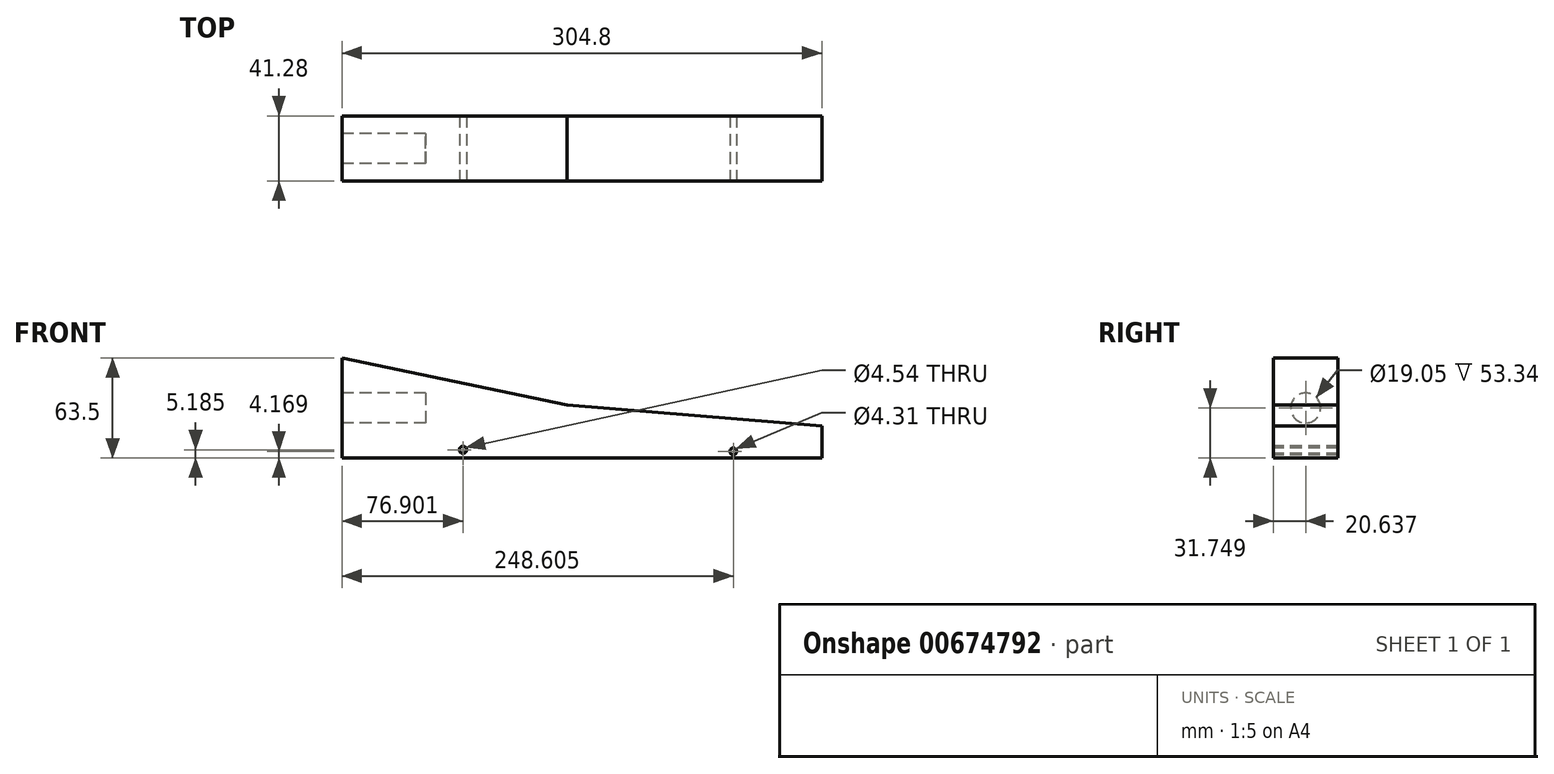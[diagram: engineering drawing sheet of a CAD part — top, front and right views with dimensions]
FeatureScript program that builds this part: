
annotation { "Feature Type Name" : "Feature", "Feature Type Description" : "" }
export const myFeature = defineFeature(function(context is Context, id is Id, definition is map)
    precondition{}
    {
        {
            var Q0;
            Q0=qCreatedBy(makeId("Front.planeOp"),FACE);
            var sketch = newSketch(context, id + "F0", { "sketchPlane" : qUnion([Q0])});
            skLineSegment(sketch, "E0", {"start": v(-67.2, 29.74) * mm, "end": v(-67.2, -33.76) * mm});
            skLineSegment(sketch, "E1", {"start": v(-67.2, -33.76) * mm, "end": v(237.6, -33.76) * mm});
            skLineSegment(sketch, "E2", {"start": v(237.6, -33.76) * mm, "end": v(237.6, -13.44) * mm});
            skLineSegment(sketch, "E3", {"start": v(237.6, -13.44) * mm, "end": v(-67.2, 29.74) * mm});
            skSolve(sketch);
        }
        {
            var Q0;
            Q0=makeQuery(id+"F0.imprint","IMPRINT",FACE,{"disambiguationData":[TD([[makeQuery(id+"F0.imprint","IMPRINT",EDGE,{"derivedFrom":sQuery(id+"F0.wireOp",EDGE,"E0")}),1.0]])]});
            extrude(context, id + "F1", {"entities" : qUnion([Q0]), "oppositeDirection" : true, "depth" : 41.27 * mm, "offsetDistance" : 25.4 * mm});
        }
        {
            var Q0;
            Q0=makeQuery(id+"F1.opExtrude","SWEPT_FACE",FACE,{"disambiguationData":[OSD([sQuery(id+"F0.wireOp",EDGE,"E0")])]});
            var sketch = newSketch(context, id + "F2", { "sketchPlane" : qUnion([Q0])});
            skCircle(sketch, "E4", {"center": v(-20.64, -2.01) * mm, "radius": 9.53 * mm});
            skPoint(sketch, "E4.centerSnap0", {"position": v(0, -2.01) * mm});
            skPoint(sketch, "E4.centerSnap1", {"position": v(-20.64, 29.74) * mm});
            skSolve(sketch);
        }
        {
            var Q0;
            Q0=makeQuery(id+"F2.imprint","IMPRINT",FACE,{"disambiguationData":[TD([[makeQuery(id+"F2.imprint","IMPRINT",EDGE,{"derivedFrom":sQuery(id+"F2.wireOp",EDGE,"E4")}),1.0]])]});
            extrude(context, id + "F3", {"entities" : qUnion([Q0]), "operationType" : NewBodyOperationType.REMOVE, "oppositeDirection" : true, "depth" : 53.34 * mm, "offsetDistance" : 25.4 * mm});
        }
        {
            var Q0;
            Q0=makeQuery(id+"F1.opExtrude","CAP_FACE",FACE,{"disambiguationData":[OSD([sQuery(id+"F0.wireOp",EDGE,"E0"),sQuery(id+"F0.wireOp",EDGE,"E1"),sQuery(id+"F0.wireOp",EDGE,"E2"),sQuery(id+"F0.wireOp",EDGE,"E3")])],"isStart":true});
            var sketch = newSketch(context, id + "F4", { "sketchPlane" : qUnion([Q0])});
            skLineSegment(sketch, "E5", {"start": v(-67.2, 29.74) * mm, "end": v(75.76, 0) * mm});
            skLineSegment(sketch, "E6", {"start": v(75.76, 0) * mm, "end": v(237.6, -13.44) * mm});
            skSolve(sketch);
        }
        {
            var Q0;
            Q0=makeQuery(id+"F4.imprint","IMPRINT",FACE,{"disambiguationData":[TD([[makeQuery(id+"F4.imprint","IMPRINT",EDGE,{"derivedFrom":sQuery(id+"F4.wireOp",EDGE,"E5")}),1.0]])]});
            extrude(context, id + "F5", {"entities" : qUnion([Q0]), "operationType" : NewBodyOperationType.REMOVE, "oppositeDirection" : true, "depth" : 55.37 * mm, "offsetDistance" : 25.4 * mm});
        }
        {
            var Q0;
            Q0=qCreatedBy(makeId("Front.planeOp"),FACE);
            var sketch = newSketch(context, id + "F6", { "sketchPlane" : qUnion([Q0])});
            skCircle(sketch, "E7", {"center": v(9.71, -28.58) * mm, "radius": 2.27 * mm});
            skCircle(sketch, "E8", {"center": v(178.37, -29.08) * mm, "radius": 2.03 * mm});
            skSolve(sketch);
        }
        {
            var Q0;
            Q0=makeQuery(id+"F6.imprint","IMPRINT",FACE,{"disambiguationData":[TD([[makeQuery(id+"F6.imprint","IMPRINT",EDGE,{"derivedFrom":sQuery(id+"F6.wireOp",EDGE,"E7")}),1.0]])]});
            extrude(context, id + "F7", {"entities" : qUnion([Q0]), "operationType" : NewBodyOperationType.REMOVE, "oppositeDirection" : true, "depth" : 106.93 * mm, "offsetDistance" : 25.4 * mm});
        }
        {
            var Q0;
            Q0=makeQuery(id+"F1.opExtrude","CAP_FACE",FACE,{"disambiguationData":[OSD([sQuery(id+"F0.wireOp",EDGE,"E0"),sQuery(id+"F0.wireOp",EDGE,"E1"),sQuery(id+"F0.wireOp",EDGE,"E2"),sQuery(id+"F0.wireOp",EDGE,"E3")])],"isStart":true});
            var sketch = newSketch(context, id + "F8", { "sketchPlane" : qUnion([Q0])});
            skCircle(sketch, "E9", {"center": v(181.41, -29.6) * mm, "radius": 2.16 * mm});
            skSolve(sketch);
        }
        {
            var Q0;
            Q0=makeQuery(id+"F8.imprint","IMPRINT",FACE,{"disambiguationData":[TD([[makeQuery(id+"F8.imprint","IMPRINT",EDGE,{"derivedFrom":sQuery(id+"F8.wireOp",EDGE,"E9")}),1.0]])]});
            extrude(context, id + "F9", {"entities" : qUnion([Q0]), "operationType" : NewBodyOperationType.REMOVE, "oppositeDirection" : true, "depth" : 91.95 * mm, "offsetDistance" : 25.4 * mm});
        }
    });
